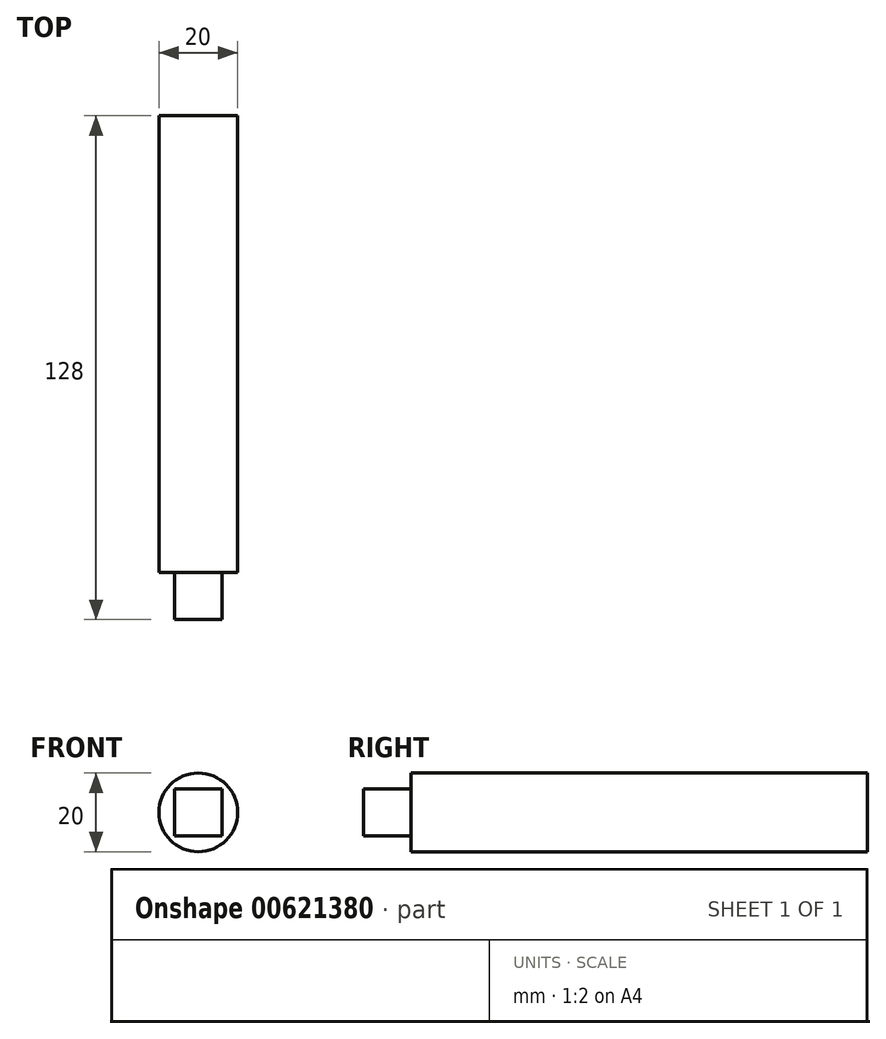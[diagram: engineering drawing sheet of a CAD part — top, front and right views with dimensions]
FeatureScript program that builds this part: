
annotation { "Feature Type Name" : "Feature", "Feature Type Description" : "" }
export const myFeature = defineFeature(function(context is Context, id is Id, definition is map)
    precondition{}
    {
        {
            var Q0;
            Q0=qCreatedBy(makeId("Front.planeOp"),FACE);
            var sketch = newSketch(context, id + "F0", { "sketchPlane" : qUnion([Q0])});
            skCircle(sketch, "E0", {"center": v(0, 0) * mm, "radius": 10 * mm});
            skSolve(sketch);
        }
        {
            var Q0;
            Q0 = qSketchRegion(id + "F0", true);
            extrude(context, id + "F1", {"entities" : qUnion([Q0]), "depth" : 116 * mm, "offsetDistance" : 25 * mm});
        }
        {
            var Q0;
            Q0=makeQuery(id+"F1.opExtrude","CAP_FACE",FACE,{"disambiguationData":[OSD([sQuery(id+"F0.wireOp",EDGE,"E0")])],"isStart":false});
            var sketch = newSketch(context, id + "F2", { "sketchPlane" : qUnion([Q0])});
            skPoint(sketch, "E1.middle", {"position": v(0, 0) * mm});
            skLineSegment(sketch, "E2.bottom", {"start": v(6, -6) * mm, "end": v(-6, -6) * mm});
            skLineSegment(sketch, "E2.top", {"start": v(6, 6) * mm, "end": v(-6, 6) * mm});
            skLineSegment(sketch, "E2.left", {"start": v(6, -6) * mm, "end": v(6, 6) * mm});
            skLineSegment(sketch, "E2.right", {"start": v(-6, -6) * mm, "end": v(-6, 6) * mm});
            skSolve(sketch);
        }
        {
            var Q0;
            Q0 = qSketchRegion(id + "F2", true);
            extrude(context, id + "F3", {"entities" : qUnion([Q0]), "operationType" : NewBodyOperationType.ADD, "depth" : 12 * mm, "offsetDistance" : 25 * mm});
        }
    });
